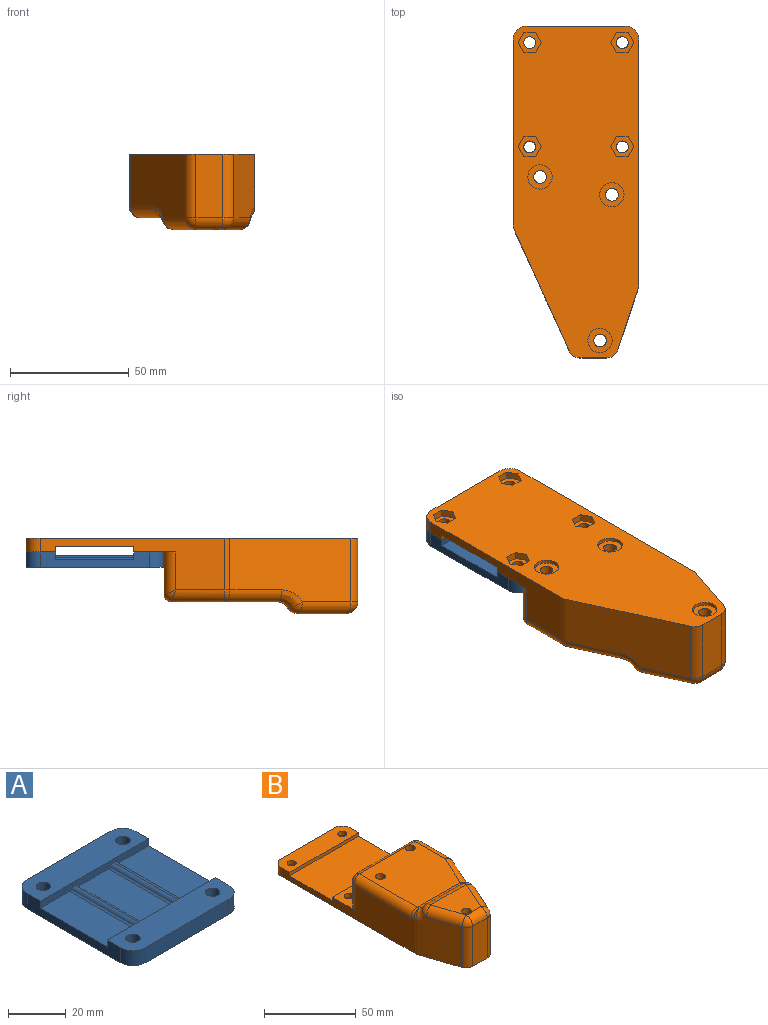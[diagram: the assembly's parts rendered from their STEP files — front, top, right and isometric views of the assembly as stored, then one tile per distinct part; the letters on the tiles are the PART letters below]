
ASSEMBLY  parts=2 mates=1
PART A: 31 faces, bbox 53.1x58x6.5 mm
  f0: plane 33x14.6mm, normal (0,0,1), area 481.8mm2, adj f1,f7,f17,f21
  f1: plane 53.1x3mm, normal (0,-1,0), area 151.6mm2, adj f0,f2,f3,f5,f7,f19,f20,f21
  f2: plane 33x15.07mm, normal (0,0,1), area 497.2mm2, adj f1,f17,f20,f25
  f3: plane 33x14.43mm, normal (0,0,1), area 476.3mm2, adj f1,f5,f17,f22
  f4: plane 41.1x6.5mm, normal (0,1,0), area 267.2mm2, adj f8,f19,f27,f30
  f5: plane 46x6.5mm, normal (-1,0,0), area 200mm2, adj f1,f3,f8,f17,f18,f19,f27,f28
  f6: plane 41.1x6.5mm, normal (0,-1,0), area 267.2mm2, adj f8,f18,f28,f29
  f7: plane 46x6.5mm, normal (1,0,0), area 200mm2, adj f0,f1,f8,f17,f18,f19,f29,f30
  f8: plane 58x53.1mm, normal (0,0,-1), area 2668.8mm2, adj f4,f5,f6,f7,f13,f14,f15,f16
  f9: cylinder r=2.5mm len=5mm, axis (0,0,-1), area 55mm2, adj f14,f19
  f10: cylinder r=2.5mm len=5mm, axis (0,0,-1), area 55mm2, adj f13,f19
  f11: cylinder r=2.5mm len=5mm, axis (0,0,-1), area 55mm2, adj f16,f18
  f12: cylinder r=2.5mm len=5mm, axis (0,0,-1), area 55mm2, adj f15,f18
  f13: cone r=2.5mm half-angle=45deg, axis (0,0,-1), area 106.6mm2, adj f8,f10
  f14: cone r=2.5mm half-angle=45deg, axis (0,0,-1), area 106.6mm2, adj f8,f9
  f15: cone r=2.5mm half-angle=45deg, axis (0,0,-1), area 106.6mm2, adj f8,f12
  f16: cone r=2.5mm half-angle=45deg, axis (0,0,-1), area 106.6mm2, adj f8,f11
  f17: plane 53.1x3mm, normal (0,1,0), area 151.6mm2, adj f0,f2,f3,f5,f7,f18,f20,f21
  f18: plane 53.1x12.5mm, normal (0,0,1), area 609mm2, adj f5,f6,f7,f11,f12,f17,f28,f29
  f19: plane 53.1x12.5mm, normal (0,0,1), area 609mm2, adj f1,f4,f5,f7,f9,f10,f27,f30
  f20: cylinder r=1mm len=33mm, axis (0,-1,0), area 34.6mm2, adj f1,f2,f17,f24
  f21: cylinder r=1mm len=33mm, axis (0,1,0), area 34.6mm2, adj f0,f1,f17,f23
  f22: cylinder r=1mm len=33mm, axis (0,-1,0), area 34.6mm2, adj f1,f3,f17,f26
  f23: cylinder r=2mm len=33mm, axis (0,1,0), area 65.9mm2, adj f1,f17,f21,f24
  f24: cylinder r=2mm len=33mm, axis (0,-1,0), area 65.9mm2, adj f1,f17,f20,f23
  f25: cylinder r=2mm len=33mm, axis (0,1,0), area 78.1mm2, adj f1,f2,f17,f26
  f26: cylinder r=2mm len=33mm, axis (0,-1,0), area 60.3mm2, adj f1,f17,f22,f25
  f27: cylinder r=6mm len=6.5mm, axis (0,0,-1), area 61.3mm2, adj f4,f5,f8,f19
  f28: cylinder r=6mm len=6.5mm, axis (0,0,1), area 61.3mm2, adj f5,f6,f8,f18
  f29: cylinder r=6mm len=6.5mm, axis (0,0,-1), area 61.3mm2, adj f6,f7,f8,f18
  f30: cylinder r=6mm len=6.5mm, axis (0,0,1), area 61.3mm2, adj f4,f7,f8,f19
PART B: 84 faces, bbox 53.1x140x31.8 mm
  f0: plane 44.6x43.1mm, normal (0,0,1), area 1768.7mm2, adj f50,f51,f58,f59,f71,f79,f81
  f1: cylinder r=2.5mm len=5mm, axis (0,0,-1), area 43.2mm2, adj f11,f37
  f2: cylinder r=2.5mm len=5mm, axis (0,0,-1), area 43.2mm2, adj f11,f30
  f3: cylinder r=2.5mm len=5mm, axis (0,0,-1), area 43.2mm2, adj f13,f23
  f4: cylinder r=2.5mm len=5mm, axis (0,0,-1), area 43.2mm2, adj f13,f16
  f5: plane 53.1x33mm, normal (0,0,1), area 1752.3mm2, adj f7,f8,f10,f12
  f6: plane 41.1x5.75mm, normal (0,1,0), area 236.3mm2, adj f9,f13,f14,f15
  f7: plane 103.19x22.34mm, normal (-1,0,0), area 1255.6mm2, adj f5,f9,f10,f11,f12,f13,f14,f62
  f8: plane 77.92x21.75mm, normal (1,0,0), area 705.2mm2, adj f5,f9,f10,f11,f12,f13,f15,f68
  f9: plane 140x53.1mm, normal (0,0,-1), area 6078.9mm2, adj f6,f7,f8,f14,f15,f17,f18,f19
  f10: plane 53.1x2.25mm, normal (0,1,0), area 119.5mm2, adj f5,f7,f8,f11
  f11: plane 53.1x17.7mm, normal (0,0,1), area 645.8mm2, adj f1,f2,f7,f8,f10,f45,f69,f83
  f12: plane 53.1x2.25mm, normal (0,-1,0), area 119.5mm2, adj f5,f7,f8,f13
  f13: plane 53.1x12.5mm, normal (0,0,1), area 609mm2, adj f3,f4,f6,f7,f8,f12,f14,f15
  f14: cylinder r=6mm len=6mm, axis (0,0,-1), area 54.2mm2, adj f6,f7,f9,f13
  f15: cylinder r=6mm len=6mm, axis (0,0,1), area 54.2mm2, adj f6,f8,f9,f13
  f16: plane 9.82x8.5mm, normal (0,0,-1), area 42.9mm2, adj f4,f17,f18,f19,f20,f21,f22
  f17: plane 4.25x3mm, normal (-0.87,-0.5,0), area 14.7mm2, adj f9,f16,f18,f22
  f18: plane 4.25x3mm, normal (-0.87,0.5,0), area 14.7mm2, adj f9,f16,f17,f19
  f19: plane 4.91x3mm, normal (0,1,0), area 14.7mm2, adj f9,f16,f18,f20
  f20: plane 4.25x3mm, normal (0.87,0.5,0), area 14.7mm2, adj f9,f16,f19,f21
  f21: plane 4.25x3mm, normal (0.87,-0.5,0), area 14.7mm2, adj f9,f16,f20,f22
  f22: plane 4.91x3mm, normal (0,-1,0), area 14.7mm2, adj f9,f16,f17,f21
  f23: plane 9.82x8.5mm, normal (0,0,-1), area 42.9mm2, adj f3,f24,f25,f26,f27,f28,f29
  f24: plane 4.25x3mm, normal (-0.87,-0.5,0), area 14.7mm2, adj f9,f23,f25,f29
  f25: plane 4.25x3mm, normal (-0.87,0.5,0), area 14.7mm2, adj f9,f23,f24,f26
  f26: plane 4.91x3mm, normal (0,1,0), area 14.7mm2, adj f9,f23,f25,f27
  f27: plane 4.25x3mm, normal (0.87,0.5,0), area 14.7mm2, adj f9,f23,f26,f28
  f28: plane 4.25x3mm, normal (0.87,-0.5,0), area 14.7mm2, adj f9,f23,f27,f29
  f29: plane 4.91x3mm, normal (0,-1,0), area 14.7mm2, adj f9,f23,f24,f28
  f30: plane 9.82x8.5mm, normal (0,0,-1), area 42.9mm2, adj f2,f31,f32,f33,f34,f35,f36
  f31: plane 4.25x3mm, normal (-0.87,-0.5,0), area 14.7mm2, adj f9,f30,f32,f36
  f32: plane 4.25x3mm, normal (-0.87,0.5,0), area 14.7mm2, adj f9,f30,f31,f33
  f33: plane 4.91x3mm, normal (0,1,0), area 14.7mm2, adj f9,f30,f32,f34
  f34: plane 4.25x3mm, normal (0.87,0.5,0), area 14.7mm2, adj f9,f30,f33,f35
  f35: plane 4.25x3mm, normal (0.87,-0.5,0), area 14.7mm2, adj f9,f30,f34,f36
  f36: plane 4.91x3mm, normal (0,-1,0), area 14.7mm2, adj f9,f30,f31,f35
  f37: plane 9.82x8.5mm, normal (0,0,-1), area 42.9mm2, adj f1,f38,f39,f40,f41,f42,f43
  f38: plane 4.25x3mm, normal (-0.87,-0.5,0), area 14.7mm2, adj f9,f37,f39,f43
  f39: plane 4.25x3mm, normal (-0.87,0.5,0), area 14.7mm2, adj f9,f37,f38,f40
  f40: plane 4.91x3mm, normal (0,1,0), area 14.7mm2, adj f9,f37,f39,f41
  f41: plane 4.25x3mm, normal (0.87,0.5,0), area 14.7mm2, adj f9,f37,f40,f42
  f42: plane 4.25x3mm, normal (0.87,-0.5,0), area 14.7mm2, adj f9,f37,f41,f43
  f43: plane 4.91x3mm, normal (0,-1,0), area 14.7mm2, adj f9,f37,f38,f42
  f44: plane 26.75x11.28mm, normal (0,-1,0), area 301.7mm2, adj f9,f61,f65,f67
  f45: plane 43.1x18mm, normal (0,1,0), area 775.8mm2, adj f11,f58,f69,f83
  f46: plane 27.46x20.54mm, normal (0,0,1), area 376mm2, adj f49,f60,f64,f65,f76
  f47: plane 51.08x26.75mm, normal (0.91,-0.41,0), area 1347.1mm2, adj f9,f60,f61,f68,f78,f79
  f48: plane 26.75x25.81mm, normal (-0.95,-0.32,0), area 712.6mm2, adj f9,f62,f64,f67,f74
  f49: cylinder r=2.67mm len=30.25mm, axis (0,0,-1), area 508.4mm2, adj f46,f57,f65
  f50: cylinder r=2.67mm len=25.25mm, axis (0,0,-1), area 424.4mm2, adj f0,f53
  f51: cylinder r=2.67mm len=25.25mm, axis (0,0,-1), area 424.4mm2, adj f0,f55,f58
  f52: cylinder r=5.12mm len=10.25mm, axis (0,0,-1), area 48.3mm2, adj f9,f53
  f53: plane 10.25x10.25mm, normal (0,0,-1), area 60mm2, adj f50,f52
  f54: cylinder r=5.12mm len=10.25mm, axis (0,0,-1), area 48.3mm2, adj f9,f55
  f55: plane 10.25x10.25mm, normal (0,0,-1), area 60mm2, adj f51,f54
  f56: cylinder r=5.12mm len=10.25mm, axis (0,0,-1), area 48.3mm2, adj f9,f57
  f57: plane 10.25x10.25mm, normal (0,0,-1), area 60mm2, adj f49,f56
  f58: cylinder r=3mm len=43.1mm, axis (1,0,0), area 202.8mm2, adj f0,f45,f51,f70,f82
  f59: cylinder r=5mm len=33.15mm, axis (-1,0,0), area 159.1mm2, adj f0,f72,f74,f76,f78
  f60: cylinder r=5mm len=22.61mm, axis (0.41,0.91,0), area 177.2mm2, adj f46,f47,f63,f77
  f61: cylinder r=5mm len=26.75mm, axis (0,0,1), area 153mm2, adj f9,f44,f47,f63
  f62: cylinder r=5mm len=22.34mm, axis (0,0,-1), area 35.9mm2, adj f7,f9,f48,f73
  f63: sphere r=5mm, area 28.6mm2, adj f60,f61,f65
  f64: cylinder r=5mm len=22.12mm, axis (-0.32,0.95,0), area 170.1mm2, adj f46,f48,f66,f75
  f65: cylinder r=5mm len=11.28mm, axis (1,0,0), area 88mm2, adj f44,f46,f49,f63,f66
  f66: sphere r=5mm, area 31.2mm2, adj f64,f65,f67
  f67: cylinder r=5mm len=26.75mm, axis (0,0,1), area 167.1mm2, adj f9,f44,f48,f66
  f68: cylinder r=5mm len=21.75mm, axis (0,0,1), area 46.4mm2, adj f8,f9,f47,f80
  f69: cylinder r=5mm len=18mm, axis (0,0,1), area 135.7mm2, adj f7,f11,f45,f70
  f70: bspline ~6.03x5mm, area 24.5mm2, adj f58,f69,f71
  f71: cylinder r=5mm len=44.6mm, axis (0,-1,0), area 344.6mm2, adj f0,f7,f70,f72
  f72: torus R=10mm, axis (-1,0,0), area 18.5mm2, adj f7,f59,f71,f73
  f73: sphere r=5mm, area 8mm2, adj f62,f72,f74
  f74: bspline ~8.55x7mm, area 43.2mm2, adj f48,f59,f73,f75
  f75: sphere r=5mm, area 29.5mm2, adj f64,f74,f76
  f76: cylinder r=5mm len=27.46mm, axis (-1,0,0), area 143.8mm2, adj f46,f59,f75,f77
  f77: sphere r=5mm, area 31.1mm2, adj f60,f76,f78
  f78: bspline ~12.34x9.62mm, area 68.9mm2, adj f47,f59,f77,f79
  f79: cylinder r=5mm len=23.95mm, axis (0.41,0.91,0), area 188.8mm2, adj f0,f47,f78,f80
  f80: sphere r=5mm, area 10.7mm2, adj f68,f79,f81
  f81: cylinder r=5mm len=22.72mm, axis (0,1,0), area 172.7mm2, adj f0,f8,f80,f82
  f82: bspline ~6.03x5mm, area 24.5mm2, adj f58,f81,f83
  f83: cylinder r=5mm len=18mm, axis (0,0,-1), area 135.7mm2, adj f8,f11,f45,f82
PLACE A rot(axis=(1,0,0),0deg) t=(0,-23,10.35)mm
PLACE B rot(axis=(0,1,0),180deg) t=(38.1,0,18.6)mm
MATE pin_slot B.f4 <-> A.f10  axis (0,0,-1) through (-0.5,18.73,14.85)mm
